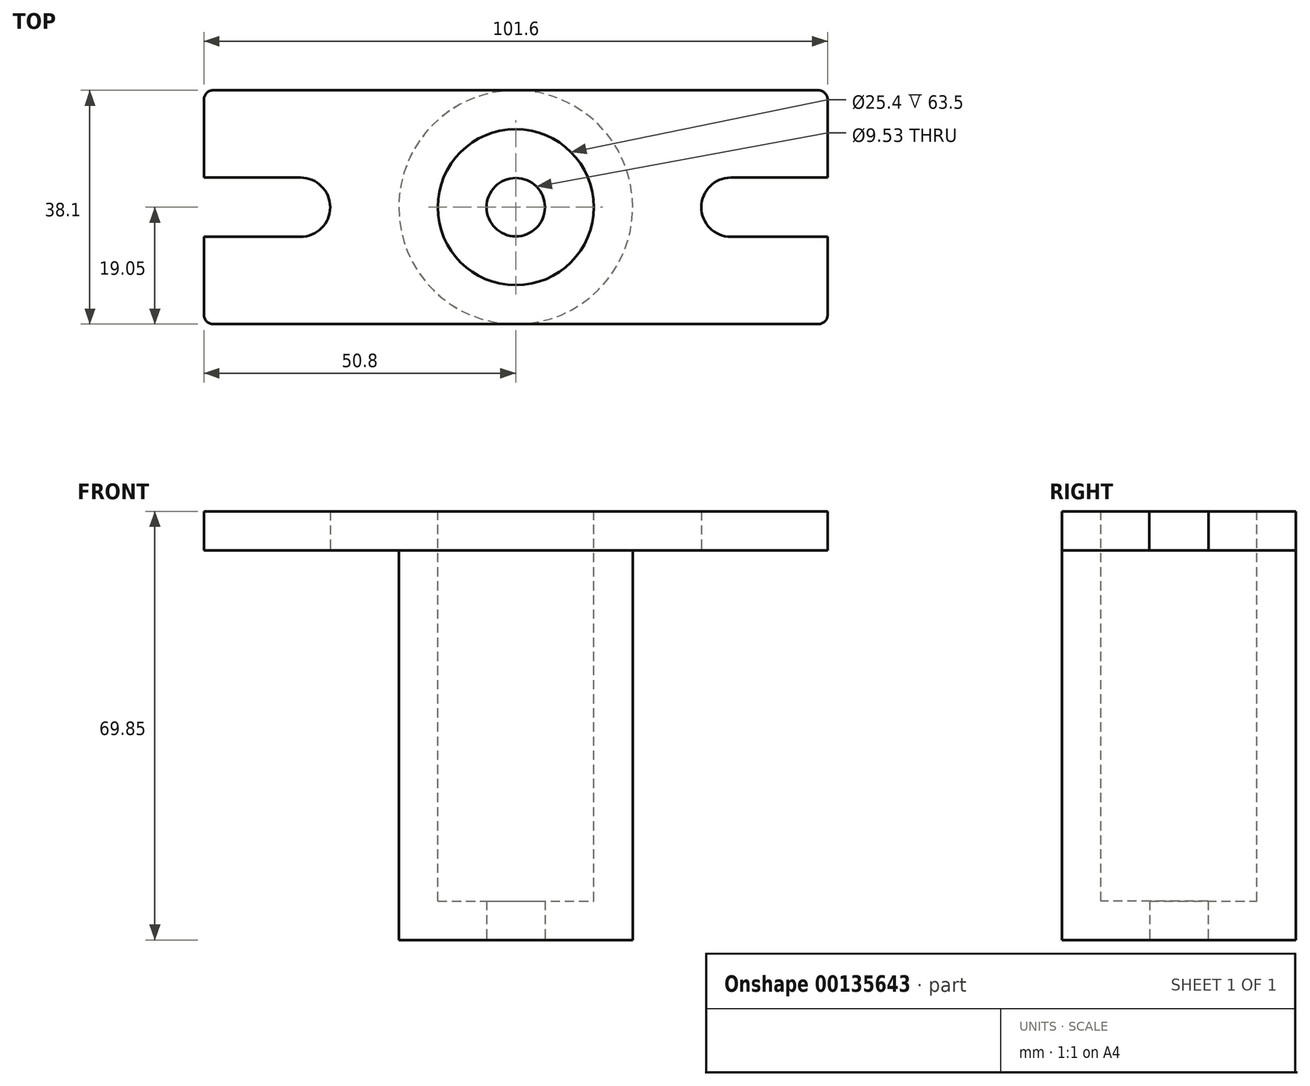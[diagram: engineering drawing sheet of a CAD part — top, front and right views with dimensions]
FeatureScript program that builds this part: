
annotation { "Feature Type Name" : "Feature", "Feature Type Description" : "" }
export const myFeature = defineFeature(function(context is Context, id is Id, definition is map)
    precondition{}
    {
        {
            var Q0;
            Q0=qCreatedBy(makeId("Top.planeOp"),FACE);
            var sketch = newSketch(context, id + "F0", { "sketchPlane" : qUnion([Q0])});
            skLineSegment(sketch, "E0", {"start": v(-86.64, 0) * mm, "end": v(77.82, 0) * mm, "construction": true});
            skLineSegment(sketch, "E1", {"start": v(-49.28, 19.05) * mm, "end": v(0, 19.05) * mm});
            skLineSegment(sketch, "E2", {"start": v(0, 19.05) * mm, "end": v(49.28, 19.05) * mm});
            skLineSegment(sketch, "E3", {"start": v(50.8, 17.53) * mm, "end": v(50.8, 4.83) * mm});
            skLineSegment(sketch, "E4", {"start": v(-50.8, 17.53) * mm, "end": v(-50.8, 4.83) * mm});
            skLineSegment(sketch, "E5", {"start": v(-50.8, 4.83) * mm, "end": v(-35.05, 4.83) * mm});
            skLineSegment(sketch, "E6", {"start": v(50.8, 4.83) * mm, "end": v(35.05, 4.83) * mm});
            skArc(sketch, "E7", {"start": v(-35.05, 4.83) * mm, "mid": v(-31.64, 3.41) * mm, "end": v(-30.23, 0) * mm});
            skArc(sketch, "E8", {"start": v(35.05, 4.83) * mm, "mid": v(31.64, 3.41) * mm, "end": v(30.23, 0) * mm});
            skPoint(sketch, "E9.visualSharp", {"position": v(-50.8, 19.05) * mm});
            skArc(sketch, "E9.filletArc", {"start": v(-49.28, 19.05) * mm, "mid": v(-50.35, 18.6) * mm, "end": v(-50.8, 17.53) * mm});
            skPoint(sketch, "E10.visualSharp", {"position": v(50.8, 19.05) * mm});
            skArc(sketch, "E10.filletArc", {"start": v(50.8, 17.53) * mm, "mid": v(50.35, 18.6) * mm, "end": v(49.28, 19.05) * mm});
            skArc(sketch, "E11.MirrorCS", {"start": v(-35.05, -4.83) * mm, "mid": v(-31.64, -3.41) * mm, "end": v(-30.23, 0) * mm});
            skLineSegment(sketch, "E12.MirrorCS", {"start": v(-50.8, -4.83) * mm, "end": v(-35.05, -4.83) * mm});
            skLineSegment(sketch, "E13.MirrorCS", {"start": v(-50.8, -17.53) * mm, "end": v(-50.8, -4.83) * mm});
            skArc(sketch, "E14.MirrorCS", {"start": v(-49.28, -19.05) * mm, "mid": v(-50.35, -18.6) * mm, "end": v(-50.8, -17.53) * mm});
            skLineSegment(sketch, "E15.MirrorCS", {"start": v(-49.28, -19.05) * mm, "end": v(0, -19.05) * mm});
            skLineSegment(sketch, "E16.MirrorCS", {"start": v(0, -19.05) * mm, "end": v(49.28, -19.05) * mm});
            skArc(sketch, "E17.MirrorCS", {"start": v(50.8, -17.53) * mm, "mid": v(50.35, -18.6) * mm, "end": v(49.28, -19.05) * mm});
            skLineSegment(sketch, "E18.MirrorCS", {"start": v(50.8, -17.53) * mm, "end": v(50.8, -4.83) * mm});
            skLineSegment(sketch, "E19.MirrorCS", {"start": v(50.8, -4.83) * mm, "end": v(35.05, -4.83) * mm});
            skArc(sketch, "E20.MirrorCS", {"start": v(35.05, -4.83) * mm, "mid": v(31.64, -3.41) * mm, "end": v(30.23, 0) * mm});
            skSolve(sketch);
        }
        {
            var Q0;
            Q0=makeQuery(id+"F0.imprint","IMPRINT",FACE,{"disambiguationData":[TD([[makeQuery(id+"F0.imprint","IMPRINT",EDGE,{"derivedFrom":sQuery(id+"F0.wireOp",EDGE,"E1")}),-1.0]])]});
            extrude(context, id + "F1", {"entities" : qUnion([Q0]), "depth" : 6.35 * mm});
        }
        {
            var Q0;
            Q0=makeQuery(id+"F1.opExtrude","CAP_FACE",FACE,{"disambiguationData":[OSD([sQuery(id+"F0.wireOp",EDGE,"E1"),sQuery(id+"F0.wireOp",EDGE,"E2"),sQuery(id+"F0.wireOp",EDGE,"E3"),sQuery(id+"F0.wireOp",EDGE,"E4"),sQuery(id+"F0.wireOp",EDGE,"E5"),sQuery(id+"F0.wireOp",EDGE,"E6"),sQuery(id+"F0.wireOp",EDGE,"E7"),sQuery(id+"F0.wireOp",EDGE,"E8"),sQuery(id+"F0.wireOp",EDGE,"E9.filletArc"),sQuery(id+"F0.wireOp",EDGE,"E10.filletArc"),sQuery(id+"F0.wireOp",EDGE,"E11.MirrorCS"),sQuery(id+"F0.wireOp",EDGE,"E12.MirrorCS"),sQuery(id+"F0.wireOp",EDGE,"E13.MirrorCS"),sQuery(id+"F0.wireOp",EDGE,"E14.MirrorCS"),sQuery(id+"F0.wireOp",EDGE,"E15.MirrorCS"),sQuery(id+"F0.wireOp",EDGE,"E16.MirrorCS"),sQuery(id+"F0.wireOp",EDGE,"E17.MirrorCS"),sQuery(id+"F0.wireOp",EDGE,"E18.MirrorCS"),sQuery(id+"F0.wireOp",EDGE,"E19.MirrorCS"),sQuery(id+"F0.wireOp",EDGE,"E20.MirrorCS")])],"isStart":false});
            var sketch = newSketch(context, id + "F2", { "sketchPlane" : qUnion([Q0])});
            skCircle(sketch, "E21", {"center": v(0, 0) * mm, "radius": 12.7 * mm});
            skSolve(sketch);
        }
        {
            var Q0;
            Q0=makeQuery(id+"F2.imprint","IMPRINT",FACE,{"disambiguationData":[TD([[makeQuery(id+"F2.imprint","IMPRINT",EDGE,{"derivedFrom":sQuery(id+"F2.wireOp",EDGE,"E21")}),1.0]])]});
            extrude(context, id + "F3", {"entities" : qUnion([Q0]), "operationType" : NewBodyOperationType.REMOVE, "oppositeDirection" : true, "depth" : 63.5 * mm});
        }
        {
            var Q0;
            Q0=makeQuery(id+"F1.opExtrude","CAP_FACE",FACE,{"disambiguationData":[OSD([sQuery(id+"F0.wireOp",EDGE,"E1"),sQuery(id+"F0.wireOp",EDGE,"E2"),sQuery(id+"F0.wireOp",EDGE,"E3"),sQuery(id+"F0.wireOp",EDGE,"E4"),sQuery(id+"F0.wireOp",EDGE,"E5"),sQuery(id+"F0.wireOp",EDGE,"E6"),sQuery(id+"F0.wireOp",EDGE,"E7"),sQuery(id+"F0.wireOp",EDGE,"E8"),sQuery(id+"F0.wireOp",EDGE,"E9.filletArc"),sQuery(id+"F0.wireOp",EDGE,"E10.filletArc"),sQuery(id+"F0.wireOp",EDGE,"E11.MirrorCS"),sQuery(id+"F0.wireOp",EDGE,"E12.MirrorCS"),sQuery(id+"F0.wireOp",EDGE,"E13.MirrorCS"),sQuery(id+"F0.wireOp",EDGE,"E14.MirrorCS"),sQuery(id+"F0.wireOp",EDGE,"E15.MirrorCS"),sQuery(id+"F0.wireOp",EDGE,"E16.MirrorCS"),sQuery(id+"F0.wireOp",EDGE,"E17.MirrorCS"),sQuery(id+"F0.wireOp",EDGE,"E18.MirrorCS"),sQuery(id+"F0.wireOp",EDGE,"E19.MirrorCS"),sQuery(id+"F0.wireOp",EDGE,"E20.MirrorCS")])],"isStart":true});
            var sketch = newSketch(context, id + "F4", { "sketchPlane" : qUnion([Q0])});
            skCircle(sketch, "E22", {"center": v(0, 0) * mm, "radius": 19.05 * mm});
            skSolve(sketch);
        }
        {
            var Q0;
            {var subQ0=sQuery(id+"F4.wireOp",EDGE,"E22");var subQ1=sQuery(id+"F0.wireOp",EDGE,"E2");var subQ2=sQuery(id+"F0.wireOp",EDGE,"E1");var subQ3=makeQuery(id+"F4.imprint","INTERSECT",VERTEX,{"derivedFrom":[makeQuery(id+"F1.opExtrude","CAP_EDGE",EDGE,{"disambiguationData":[OSD([subQ2,subQ1])],"isStart":true}),subQ0]});Q0=makeQuery(id+"F4.imprint","IMPRINT",FACE,{"disambiguationData":[TD([[makeQuery(id+"F4.imprint","IMPRINT",EDGE,{"disambiguationData":[TD([[subQ3,1.0]])],"derivedFrom":subQ0}),1.0]])]});}
            extrude(context, id + "F5", {"entities" : qUnion([Q0]), "operationType" : NewBodyOperationType.ADD, "depth" : 63.5 * mm});
        }
        {
            var Q0;
            Q0=makeQuery(id+"F5.opExtrude","CAP_FACE",FACE,{"disambiguationData":[OSD([sQuery(id+"F0.wireOp",EDGE,"E1"),sQuery(id+"F0.wireOp",EDGE,"E2"),sQuery(id+"F0.wireOp",EDGE,"E3"),sQuery(id+"F0.wireOp",EDGE,"E4"),sQuery(id+"F0.wireOp",EDGE,"E5"),sQuery(id+"F0.wireOp",EDGE,"E6"),sQuery(id+"F0.wireOp",EDGE,"E7"),sQuery(id+"F0.wireOp",EDGE,"E8"),sQuery(id+"F0.wireOp",EDGE,"E9.filletArc"),sQuery(id+"F0.wireOp",EDGE,"E10.filletArc"),sQuery(id+"F0.wireOp",EDGE,"E11.MirrorCS"),sQuery(id+"F0.wireOp",EDGE,"E12.MirrorCS"),sQuery(id+"F0.wireOp",EDGE,"E13.MirrorCS"),sQuery(id+"F0.wireOp",EDGE,"E14.MirrorCS"),sQuery(id+"F0.wireOp",EDGE,"E15.MirrorCS"),sQuery(id+"F0.wireOp",EDGE,"E16.MirrorCS"),sQuery(id+"F0.wireOp",EDGE,"E17.MirrorCS"),sQuery(id+"F0.wireOp",EDGE,"E18.MirrorCS"),sQuery(id+"F0.wireOp",EDGE,"E19.MirrorCS"),sQuery(id+"F0.wireOp",EDGE,"E20.MirrorCS"),sQuery(id+"F2.wireOp",EDGE,"E21"),sQuery(id+"F4.wireOp",EDGE,"E22")])],"isStart":false});
            var sketch = newSketch(context, id + "F6", { "sketchPlane" : qUnion([Q0])});
            skCircle(sketch, "E23", {"center": v(0, 0) * mm, "radius": 4.76 * mm});
            skSolve(sketch);
        }
        {
            var Q0;
            Q0=makeQuery(id+"F6.imprint","IMPRINT",FACE,{"disambiguationData":[TD([[makeQuery(id+"F6.imprint","IMPRINT",EDGE,{"derivedFrom":sQuery(id+"F6.wireOp",EDGE,"E23")}),-1.0]])]});
            extrude(context, id + "F7", {"entities" : qUnion([Q0]), "operationType" : NewBodyOperationType.ADD, "oppositeDirection" : true, "depth" : 6.35 * mm});
        }
    });
